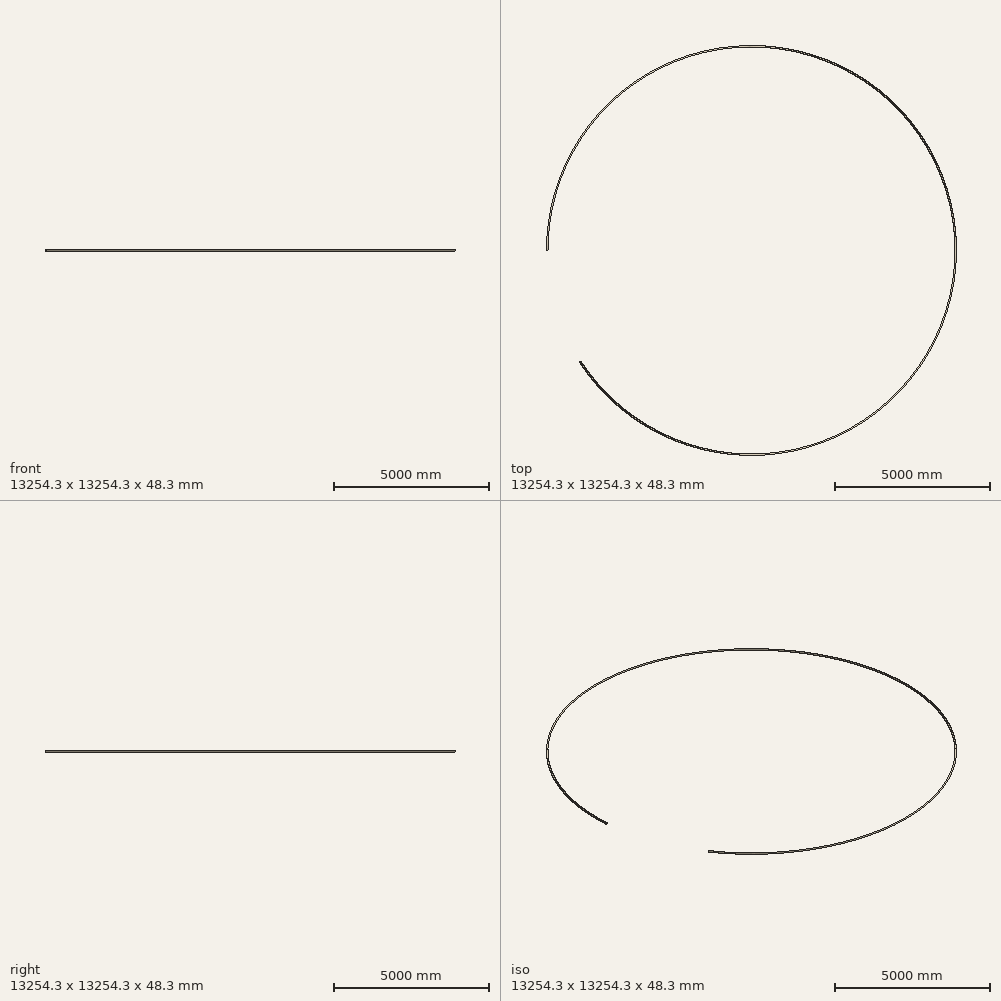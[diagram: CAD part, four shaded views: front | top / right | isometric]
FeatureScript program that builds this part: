
annotation { "Feature Type Name" : "Feature", "Feature Type Description" : "" }
export const myFeature = defineFeature(function(context is Context, id is Id, definition is map)
    precondition{}
    {
        {
            var Q0;
            Q0=qCreatedBy(makeId("Front.planeOp"),FACE);
            var sketch = newSketch(context, id + "F0", { "sketchPlane" : qUnion([Q0])});
            skCircle(sketch, "E0", {"center": v(0, 0) * mm, "radius": 24.13 * mm});
            skLineSegment(sketch, "E1", {"start": v(0, 0) * mm, "end": v(6603, 0) * mm, "construction": true});
            skLineSegment(sketch, "E2", {"start": v(6603, 0) * mm, "end": v(6603, -100) * mm, "construction": true});
            skCircle(sketch, "E3.0", {"center": v(0, 0) * mm, "radius": 21.36 * mm});
            skSolve(sketch);
        }
        {
            var Q0;
            Q0=makeQuery(id+"F0.imprint","IMPRINT",FACE,{"disambiguationData":[TD([[makeQuery(id+"F0.imprint","IMPRINT",EDGE,{"derivedFrom":sQuery(id+"F0.wireOp",EDGE,"E0")}),1.0]])]});
            var Q1;
            Q1=sQuery(id+"F0.wireOp",EDGE,"E2");
            revolve(context, id + "F1", {"surfaceOperationType" : NewSurfaceOperationType.NEW, "entities" : qUnion([Q0]), "axis" : qUnion([Q1]), "revolveType" : RevolveType.ONE_DIRECTION, "angle" : 327 * degree});
        }
    });
